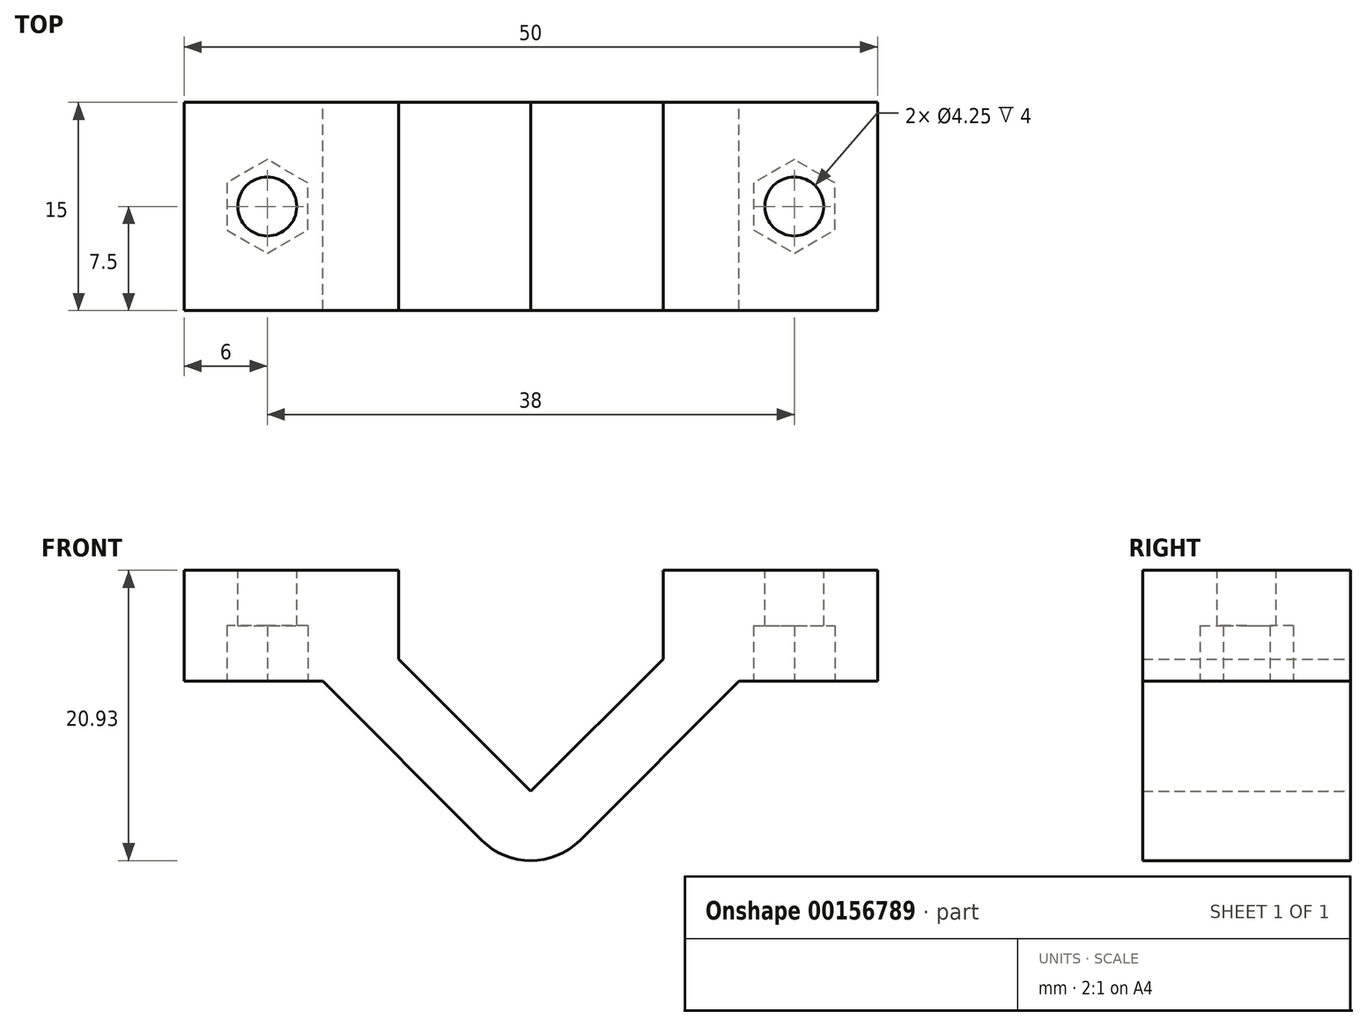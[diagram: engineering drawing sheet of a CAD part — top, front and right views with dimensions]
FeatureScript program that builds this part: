
annotation { "Feature Type Name" : "Feature", "Feature Type Description" : "" }
export const myFeature = defineFeature(function(context is Context, id is Id, definition is map)
    precondition{}
    {
        {
            var Q0;
            Q0=qCreatedBy(makeId("Front.planeOp"),FACE);
            var sketch = newSketch(context, id + "F0", { "sketchPlane" : qUnion([Q0])});
            skLineSegment(sketch, "E0.bottom", {"start": v(7.5, -12.82) * mm, "end": v(-7.5, -12.82) * mm, "construction": true});
            skLineSegment(sketch, "E0.top", {"start": v(15, 12.82) * mm, "end": v(9.55, 12.82) * mm});
            skLineSegment(sketch, "E0.right", {"start": v(-15, 4.82) * mm, "end": v(-15, 4.82) * mm});
            skPoint(sketch, "E0.middle", {"position": v(0, 0) * mm});
            skLineSegment(sketch, "E1", {"start": v(9.55, 6.43) * mm, "end": v(0, -3.11) * mm});
            skLineSegment(sketch, "E2", {"start": v(0, -3.11) * mm, "end": v(-9.55, 6.43) * mm});
            skLineSegment(sketch, "E3", {"start": v(-15, 4.82) * mm, "end": v(-7.5, -2.68) * mm});
            skLineSegment(sketch, "E4", {"start": v(-7.5, -2.68) * mm, "end": v(-7.5, -12.82) * mm, "construction": true});
            skLineSegment(sketch, "E5.MirrorCS", {"start": v(15, 4.82) * mm, "end": v(7.5, -2.68) * mm});
            skLineSegment(sketch, "E6.MirrorCS", {"start": v(7.5, -2.68) * mm, "end": v(7.5, -12.82) * mm, "construction": true});
            skPoint(sketch, "E7.orphan", {"position": v(-15, -12.82) * mm});
            skPoint(sketch, "E8.orphan", {"position": v(15, -12.82) * mm});
            skLineSegment(sketch, "E9", {"start": v(-7.5, -2.68) * mm, "end": v(0, -10.18) * mm});
            skLineSegment(sketch, "E10", {"start": v(0, -10.18) * mm, "end": v(7.5, -2.68) * mm});
            skLineSegment(sketch, "E11", {"start": v(-15, 12.82) * mm, "end": v(-25, 12.82) * mm});
            skLineSegment(sketch, "E12", {"start": v(-25, 12.82) * mm, "end": v(-25, 4.82) * mm});
            skLineSegment(sketch, "E13", {"start": v(-25, 4.82) * mm, "end": v(-15, 4.82) * mm});
            skLineSegment(sketch, "E14.MirrorCS", {"start": v(15, 12.82) * mm, "end": v(25, 12.82) * mm});
            skPoint(sketch, "E15.MirrorP", {"position": v(30.32, -12.7) * mm});
            skLineSegment(sketch, "E16", {"start": v(15, 4.82) * mm, "end": v(25, 4.82) * mm});
            skLineSegment(sketch, "E17", {"start": v(-19, 12.82) * mm, "end": v(-19, 4.82) * mm, "construction": true});
            skLineSegment(sketch, "E18", {"start": v(25, 4.82) * mm, "end": v(25, 12.82) * mm});
            skLineSegment(sketch, "E19", {"start": v(-9.55, 6.43) * mm, "end": v(-9.55, 12.82) * mm});
            skLineSegment(sketch, "E20.MirrorCS", {"start": v(9.55, 6.43) * mm, "end": v(9.55, 12.82) * mm});
            skLineSegment(sketch, "E21.trimOffspring", {"start": v(-9.55, 12.82) * mm, "end": v(-15, 12.82) * mm});
            skPoint(sketch, "E22.end.orphan", {"position": v(-8, 8) * mm});
            skPoint(sketch, "E23.start.orphan", {"position": v(8, 8) * mm});
            skSolve(sketch);
        }
        {
            var Q0;
            Q0=qSketchRegion(id+"F0",true);
            extrude(context, id + "F1", {"entities" : qUnion([Q0]), "depth" : 15 * mm});
        }
        {
            var Q0;
            Q0=makeQuery(id+"F1.opExtrude","SWEPT_FACE",FACE,{"disambiguationData":[OSD([sQuery(id+"F0.wireOp",EDGE,"E0.top"),sQuery(id+"F0.wireOp",EDGE,"E11"),sQuery(id+"F0.wireOp",EDGE,"E14.MirrorCS")])]});
            var sketch = newSketch(context, id + "F2", { "sketchPlane" : qUnion([Q0])});
            skCircle(sketch, "E24", {"center": v(-19, -7.5) * mm, "radius": 2.12 * mm});
            skCircle(sketch, "E25", {"center": v(19, -7.5) * mm, "radius": 2.12 * mm});
            skSolve(sketch);
        }
        {
            var Q0;
            Q0=qSketchRegion(id+"F2",true);
            extrude(context, id + "F3", {"entities" : qUnion([Q0]), "operationType" : NewBodyOperationType.REMOVE, "oppositeDirection" : true, "depth" : 25 * mm});
        }
        {
            var Q0;
            Q0=makeQuery(id+"F1.opExtrude","SWEPT_FACE",FACE,{"disambiguationData":[OSD([sQuery(id+"F0.wireOp",EDGE,"E13")])]});
            var sketch = newSketch(context, id + "F4", { "sketchPlane" : qUnion([Q0])});
            skCircle(sketch, "E26.cCircle", {"center": v(-19, 7.5) * mm, "radius": 2.93 * mm, "construction": true});
            skLineSegment(sketch, "E26.0", {"start": v(-21.93, 5.81) * mm, "end": v(-21.93, 9.19) * mm});
            skLineSegment(sketch, "E26.1", {"start": v(-21.93, 9.19) * mm, "end": v(-19, 10.88) * mm});
            skLineSegment(sketch, "E26.2", {"start": v(-19, 10.88) * mm, "end": v(-16.07, 9.19) * mm});
            skLineSegment(sketch, "E26.3", {"start": v(-16.07, 9.19) * mm, "end": v(-16.07, 5.81) * mm});
            skLineSegment(sketch, "E26.4", {"start": v(-16.07, 5.81) * mm, "end": v(-19, 4.12) * mm});
            skLineSegment(sketch, "E26.5", {"start": v(-19, 4.12) * mm, "end": v(-21.93, 5.81) * mm});
            skPoint(sketch, "E26.0.midPoint", {"position": v(-21.93, 7.5) * mm});
            skCircle(sketch, "E27.cCircle", {"center": v(19, 7.5) * mm, "radius": 2.92 * mm, "construction": true});
            skLineSegment(sketch, "E27.0", {"start": v(21.93, 9.19) * mm, "end": v(21.93, 5.81) * mm});
            skLineSegment(sketch, "E27.1", {"start": v(21.93, 5.81) * mm, "end": v(19, 4.12) * mm});
            skLineSegment(sketch, "E27.2", {"start": v(19, 4.12) * mm, "end": v(16.07, 5.81) * mm});
            skLineSegment(sketch, "E27.3", {"start": v(16.07, 5.81) * mm, "end": v(16.07, 9.19) * mm});
            skLineSegment(sketch, "E27.4", {"start": v(16.07, 9.19) * mm, "end": v(19, 10.88) * mm});
            skLineSegment(sketch, "E27.5", {"start": v(19, 10.88) * mm, "end": v(21.93, 9.19) * mm});
            skPoint(sketch, "E27.0.midPoint", {"position": v(21.93, 7.5) * mm});
            skSolve(sketch);
        }
        {
            var Q0;
            Q0=qSketchRegion(id+"F4",true);
            extrude(context, id + "F5", {"entities" : qUnion([Q0]), "operationType" : NewBodyOperationType.REMOVE, "oppositeDirection" : true, "depth" : 4 * mm});
        }
        {
            var Q0;
            Q0=makeQuery(id+"F1.opExtrude","SWEPT_EDGE",EDGE,{"disambiguationData":[OSD([sQuery(id+"F0.wireOp",EDGE,"E9"),sQuery(id+"F0.wireOp",EDGE,"E10")])]});
            var Q1;
            Q1=makeQuery(id+"F1.opExtrude","SWEPT_EDGE",EDGE,{"disambiguationData":[OSD([sQuery(id+"F0.wireOp",EDGE,"2255555c-475c-40c7-8031-827bdf42753017.MirrorCS"),sQuery(id+"F0.wireOp",EDGE,"2255555c-475c-40c7-8031-827bdf42753018.MirrorCS")])]});
            fillet(context, id + "F6", {"entities" : qUnion([Q0, Q1]), "radius" : 5 * mm, "tangentPropagation" : true, "allowEdgeOverflow" : false});
        }
        {
            var Q0;
            Q0=makeQuery(id+"F5.boolean.opBoolean","COPY",FACE,{"derivedFrom":makeQuery(id+"F5.opExtrude","CAP_FACE",FACE,{"disambiguationData":[OSD([sQuery(id+"F4.wireOp",EDGE,"E26.0"),sQuery(id+"F4.wireOp",EDGE,"E26.1"),sQuery(id+"F4.wireOp",EDGE,"E26.2"),sQuery(id+"F4.wireOp",EDGE,"E26.3"),sQuery(id+"F4.wireOp",EDGE,"E26.4"),sQuery(id+"F4.wireOp",EDGE,"E26.5")])],"isStart":false})});
            var sketch = newSketch(context, id + "F7", { "sketchPlane" : qUnion([Q0])});
            skCircle(sketch, "E28.cCircle", {"center": v(-19, 7.5) * mm, "radius": 2.92 * mm, "construction": true});
            skLineSegment(sketch, "E28.0", {"start": v(-21.93, 5.81) * mm, "end": v(-21.93, 9.19) * mm});
            skLineSegment(sketch, "E28.1", {"start": v(-21.93, 9.19) * mm, "end": v(-19, 10.88) * mm});
            skLineSegment(sketch, "E28.2", {"start": v(-19, 10.88) * mm, "end": v(-16.07, 9.19) * mm});
            skLineSegment(sketch, "E28.3", {"start": v(-16.08, 9.19) * mm, "end": v(-16.08, 5.81) * mm});
            skLineSegment(sketch, "E28.4", {"start": v(-16.07, 5.81) * mm, "end": v(-19, 4.12) * mm});
            skLineSegment(sketch, "E28.5", {"start": v(-19, 4.12) * mm, "end": v(-21.92, 5.81) * mm});
            skPoint(sketch, "E28.0.midPoint", {"position": v(-21.93, 7.5) * mm});
            skSolve(sketch);
        }
        {
            var Q0;
            Q0=qSketchRegion(id+"F7",true);
            extrude(context, id + "F8", {"entities" : qUnion([Q0]), "operationType" : NewBodyOperationType.REMOVE, "depth" : 25 * mm});
        }
    });
